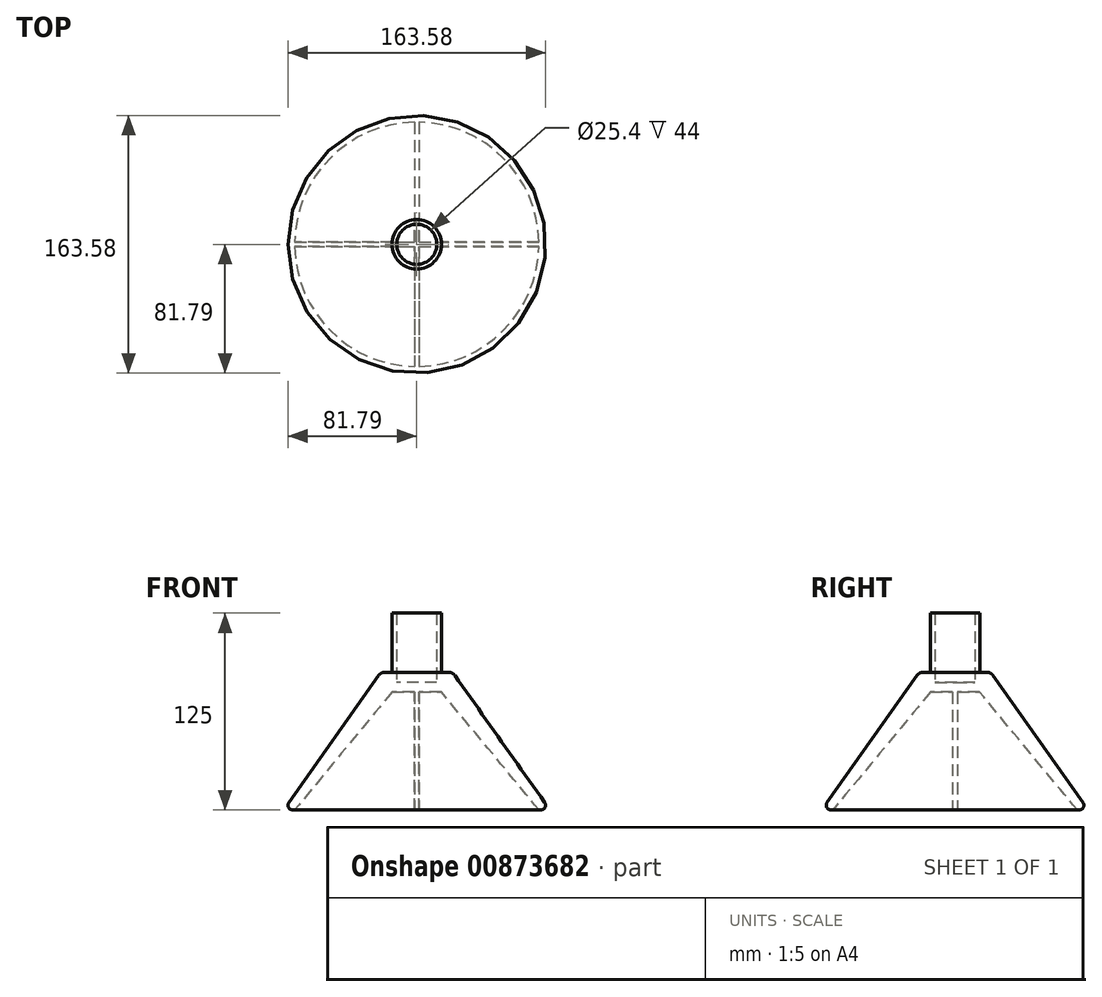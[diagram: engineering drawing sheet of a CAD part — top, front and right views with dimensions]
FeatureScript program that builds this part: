
annotation { "Feature Type Name" : "Feature", "Feature Type Description" : "" }
export const myFeature = defineFeature(function(context is Context, id is Id, definition is map)
    precondition{}
    {
        {
            var Q0;
            Q0=qCreatedBy(makeId("Top.planeOp"),FACE);
            var sketch = newSketch(context, id + "F0", { "sketchPlane" : qUnion([Q0])});
            skCircle(sketch, "E0", {"center": v(0, 0) * mm, "radius": 15.7 * mm});
            skCircle(sketch, "E1", {"center": v(0, 0) * mm, "radius": 12.7 * mm});
            skSolve(sketch);
        }
        {
            var Q0;
            Q0=makeQuery(id+"F0.imprint","IMPRINT",FACE,{"disambiguationData":[TD([[makeQuery(id+"F0.imprint","IMPRINT",EDGE,{"derivedFrom":sQuery(id+"F0.wireOp",EDGE,"E0")}),1.0]])]});
            extrude(context, id + "F1", {"entities" : qUnion([Q0]), "depth" : 50 * mm, "offsetDistance" : 25 * mm});
        }
        {
            var Q0;
            Q0=qCreatedBy(makeId("Right.planeOp"),FACE);
            var sketch = newSketch(context, id + "F2", { "sketchPlane" : qUnion([Q0])});
            skLineSegment(sketch, "E2", {"start": v(15.7, 12.5) * mm, "end": v(22.7, 12.5) * mm});
            skLineSegment(sketch, "E3", {"start": v(22.7, 12.5) * mm, "end": v(84.59, -75) * mm});
            skLineSegment(sketch, "E4", {"start": v(84.59, -75) * mm, "end": v(77.59, -75) * mm});
            skLineSegment(sketch, "E5", {"start": v(77.59, -75) * mm, "end": v(15.7, 0) * mm});
            skLineSegment(sketch, "E6", {"start": v(15.7, 0) * mm, "end": v(15.7, 12.5) * mm});
            skLineSegment(sketch, "E7", {"start": v(0, -24.87) * mm, "end": v(0, -52.77) * mm});
            skSolve(sketch);
        }
        {
            var Q0;
            Q0=makeQuery(id+"F2.imprint","IMPRINT",FACE,{"disambiguationData":[TD([[makeQuery(id+"F2.imprint","IMPRINT",EDGE,{"derivedFrom":sQuery(id+"F2.wireOp",EDGE,"E2")}),-1.0]])]});
            var Q1;
            Q1=sQuery(id+"F2.wireOp",EDGE,"E7");
            revolve(context, id + "F3", {"operationType" : NewBodyOperationType.ADD, "surfaceOperationType" : NewSurfaceOperationType.NEW, "entities" : qUnion([Q0]), "axis" : qUnion([Q1]), "revolveType" : RevolveType.FULL});
        }
        {
            var Q0;
            Q0=makeQuery(id+"F1.opExtrude","CAP_FACE",FACE,{"disambiguationData":[OSD([sQuery(id+"F0.wireOp",EDGE,"E0"),sQuery(id+"F0.wireOp",EDGE,"E1")])],"isStart":true});
            var sketch = newSketch(context, id + "F4", { "sketchPlane" : qUnion([Q0])});
            skCircle(sketch, "E8", {"center": v(0, 0) * mm, "radius": 12.7 * mm});
            skSolve(sketch);
        }
        {
            var Q0;
            Q0 = qSketchRegion(id + "F4", true);
            extrude(context, id + "F5", {"entities" : qUnion([Q0]), "operationType" : NewBodyOperationType.ADD, "oppositeDirection" : true, "depth" : 6 * mm, "offsetDistance" : 25 * mm});
        }
        {
            var Q0;
            Q0=qCreatedBy(makeId("Right.planeOp"),FACE);
            var sketch = newSketch(context, id + "F6", { "sketchPlane" : qUnion([Q0])});
            skLineSegment(sketch, "E9", {"start": v(15.7, 0) * mm, "end": v(77.59, -75) * mm});
            skLineSegment(sketch, "E10", {"start": v(77.59, -75) * mm, "end": v(0, -75) * mm});
            skLineSegment(sketch, "E11", {"start": v(0, 0) * mm, "end": v(15.7, 0) * mm});
            skLineSegment(sketch, "E12.MirrorCS", {"start": v(-15.7, 0) * mm, "end": v(-77.59, -75) * mm});
            skLineSegment(sketch, "E13.MirrorCS", {"start": v(-77.59, -75) * mm, "end": v(0, -75) * mm});
            skLineSegment(sketch, "E14", {"start": v(-15.7, 0) * mm, "end": v(15.7, 0) * mm});
            skSolve(sketch);
        }
        {
            var Q0;
            Q0 = qSketchRegion(id + "F6", true);
            extrude(context, id + "F7", {"entities" : qUnion([Q0]), "operationType" : NewBodyOperationType.ADD, "endBound" : BoundingType.SYMMETRIC, "depth" : 3 * mm, "offsetDistance" : 25 * mm});
        }
        {
            var Q0;
            Q0=qCreatedBy(makeId("Front.planeOp"),FACE);
            var sketch = newSketch(context, id + "F8", { "sketchPlane" : qUnion([Q0])});
            skLineSegment(sketch, "E15", {"start": v(15.7, 0) * mm, "end": v(77.59, -75) * mm});
            skLineSegment(sketch, "E16", {"start": v(77.59, -75) * mm, "end": v(0, -75) * mm});
            skLineSegment(sketch, "E17.MirrorCS", {"start": v(-77.59, -75) * mm, "end": v(0, -75) * mm});
            skLineSegment(sketch, "E18.MirrorCS", {"start": v(-15.7, 0) * mm, "end": v(-77.59, -75) * mm});
            skLineSegment(sketch, "E19", {"start": v(-15.7, 0) * mm, "end": v(15.7, 0) * mm});
            skSolve(sketch);
        }
        {
            var Q0;
            Q0 = qSketchRegion(id + "F8", true);
            extrude(context, id + "F9", {"entities" : qUnion([Q0]), "operationType" : NewBodyOperationType.ADD, "endBound" : BoundingType.SYMMETRIC, "depth" : 3 * mm, "offsetDistance" : 25 * mm});
        }
        {
            var Q0;
            Q0=makeQuery(id+"F3.opRevolve","SWEPT_EDGE",EDGE,{"disambiguationData":[OSD([sQuery(id+"F2.wireOp",EDGE,"E2"),sQuery(id+"F2.wireOp",EDGE,"E3")])]});
            fillet(context, id + "F10", {"entities" : qUnion([Q0]), "radius" : 5 * mm, "tangentPropagation" : true, "allowEdgeOverflow" : false});
        }
        {
            var Q0;
            Q0=makeQuery(id+"F3.opRevolve","SWEPT_EDGE",EDGE,{"disambiguationData":[OSD([sQuery(id+"F2.wireOp",EDGE,"E3"),sQuery(id+"F2.wireOp",EDGE,"E4")])]});
            fillet(context, id + "F11", {"entities" : qUnion([Q0]), "radius" : 3 * mm, "tangentPropagation" : true, "allowEdgeOverflow" : false});
        }
    });
